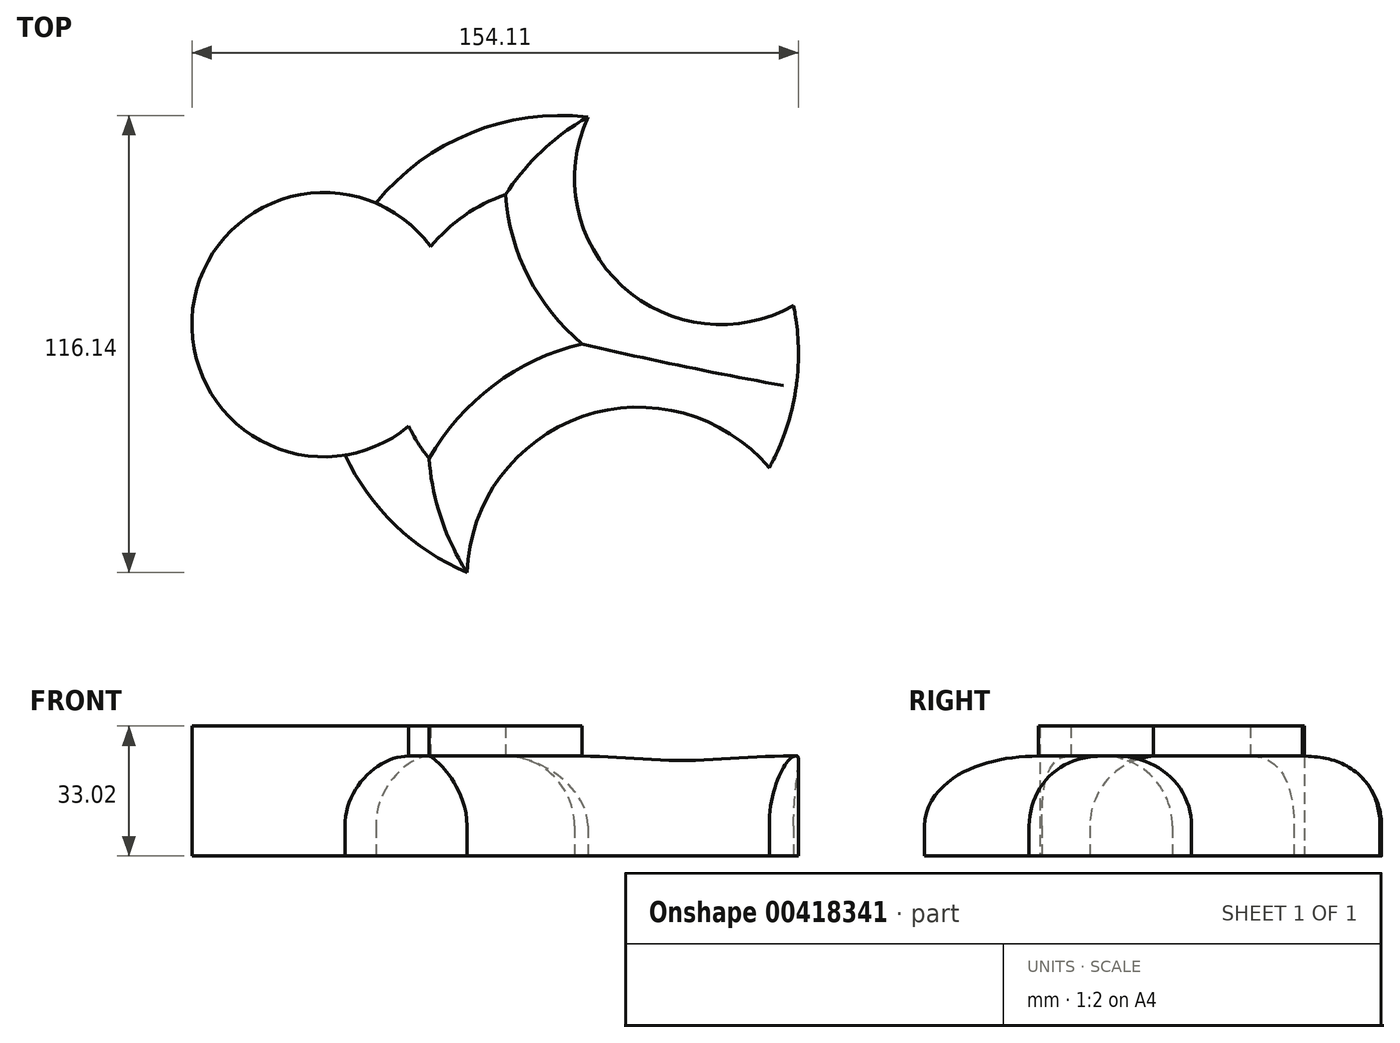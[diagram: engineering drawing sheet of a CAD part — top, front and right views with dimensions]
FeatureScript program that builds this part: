
annotation { "Feature Type Name" : "Feature", "Feature Type Description" : "" }
export const myFeature = defineFeature(function(context is Context, id is Id, definition is map)
    precondition{}
    {
        {
            var Q0;
            Q0=qCreatedBy(makeId("Top.planeOp"),FACE);
            var sketch = newSketch(context, id + "F0", { "sketchPlane" : qUnion([Q0])});
            skCircle(sketch, "E0", {"center": v(0, 0) * mm, "radius": 60.5 * mm});
            skCircle(sketch, "E1", {"center": v(40.86, 44.6) * mm, "radius": 37.24 * mm});
            skCircle(sketch, "E2", {"center": v(19.8, -57.16) * mm, "radius": 43.54 * mm});
            skCircle(sketch, "E3", {"center": v(-60.05, 7.34) * mm, "radius": 33.58 * mm});
            skSolve(sketch);
        }
        {
            var Q0;
            {var subQ0=sQuery(id+"F0.wireOp",EDGE,"E1");var subQ1=sQuery(id+"F0.wireOp",EDGE,"E0");var subQ8=makeQuery(id+"F0.imprint","INTERSECT",VERTEX,{"disambiguationData":[OD(0.0)],"derivedFrom":[subQ1,subQ0]});Q0=makeQuery(id+"F0.imprint","IMPRINT",FACE,{"disambiguationData":[TD([[makeQuery(id+"F0.imprint","IMPRINT",EDGE,{"disambiguationData":[TD([[subQ8,-1.0]])],"derivedFrom":subQ1}),1.0]])]});}
            var Q1;
            {var subQ0=sQuery(id+"F0.wireOp",EDGE,"E3");var subQ1=sQuery(id+"F0.wireOp",EDGE,"E0");var subQ2=makeQuery(id+"F0.imprint","INTERSECT",VERTEX,{"disambiguationData":[OD(0.0)],"derivedFrom":[subQ1,subQ0]});Q1=makeQuery(id+"F0.imprint","IMPRINT",FACE,{"disambiguationData":[TD([[makeQuery(id+"F0.imprint","IMPRINT",EDGE,{"disambiguationData":[TD([[subQ2,-1.0]])],"derivedFrom":subQ1}),-1.0]])]});}
            var Q2;
            {var subQ0=sQuery(id+"F0.wireOp",EDGE,"E3");var subQ1=sQuery(id+"F0.wireOp",EDGE,"E0");var subQ2=makeQuery(id+"F0.imprint","INTERSECT",VERTEX,{"disambiguationData":[OD(0.0)],"derivedFrom":[subQ1,subQ0]});Q2=makeQuery(id+"F0.imprint","IMPRINT",FACE,{"disambiguationData":[TD([[makeQuery(id+"F0.imprint","IMPRINT",EDGE,{"disambiguationData":[TD([[subQ2,-1.0]])],"derivedFrom":subQ1}),1.0]])]});}
            extrude(context, id + "F1", {"entities" : qUnion([Q0, Q1, Q2]), "depth" : 25.4 * mm});
        }
        {
            var Q0;
            Q0=makeQuery(id+"F1.opExtrude","CAP_EDGE",EDGE,{"disambiguationData":[OSD([sQuery(id+"F0.wireOp",EDGE,"E2")])],"isStart":false});
            var Q1;
            Q1=makeQuery(id+"F1.opExtrude","CAP_EDGE",EDGE,{"disambiguationData":[OSD([sQuery(id+"F0.wireOp",EDGE,"E1")])],"isStart":false});
            var Q2;
            {var subQ0=sQuery(id+"F0.wireOp",EDGE,"E0");Q2=makeQuery(id+"F1.opExtrude","CAP_EDGE",EDGE,{"disambiguationData":[OSD([subQ0]),TDD([makeQuery(id+"F0.imprint","IMPRINT",EDGE,{"disambiguationData":[TD([[makeQuery(id+"F0.imprint","INTERSECT",VERTEX,{"disambiguationData":[OD(1.0)],"derivedFrom":[subQ0,sQuery(id+"F0.wireOp",EDGE,"E3")]}),-1.0]])],"derivedFrom":subQ0})])],"isStart":false});}
            var Q3;
            {var subQ0=sQuery(id+"F0.wireOp",EDGE,"E0");Q3=makeQuery(id+"F1.opExtrude","CAP_EDGE",EDGE,{"disambiguationData":[OSD([subQ0]),TDD([makeQuery(id+"F0.imprint","IMPRINT",EDGE,{"disambiguationData":[TD([[makeQuery(id+"F0.imprint","INTERSECT",VERTEX,{"disambiguationData":[OD(0.0)],"derivedFrom":[subQ0,sQuery(id+"F0.wireOp",EDGE,"E1")]}),-1.0]])],"derivedFrom":subQ0})])],"isStart":false});}
            fillet(context, id + "F2", {"entities" : qUnion([Q0, Q1, Q2, Q3]), "radius" : 17.78 * mm, "tangentPropagation" : true, "allowEdgeOverflow" : false});
        }
        {
            var Q0;
            Q0=makeQuery(id+"F2.opFillet","SPLIT",FACE,{"disambiguationData":[OD(0.0)],"derivedFrom":makeQuery(id+"F1.opExtrude","CAP_FACE",FACE,{"disambiguationData":[OSD([sQuery(id+"F0.wireOp",EDGE,"E0"),sQuery(id+"F0.wireOp",EDGE,"E1"),sQuery(id+"F0.wireOp",EDGE,"E2"),sQuery(id+"F0.wireOp",EDGE,"E3")])],"isStart":false})});
            extrude(context, id + "F3", {"entities" : qUnion([Q0]), "operationType" : NewBodyOperationType.ADD, "depth" : 7.62 * mm});
        }
    });
